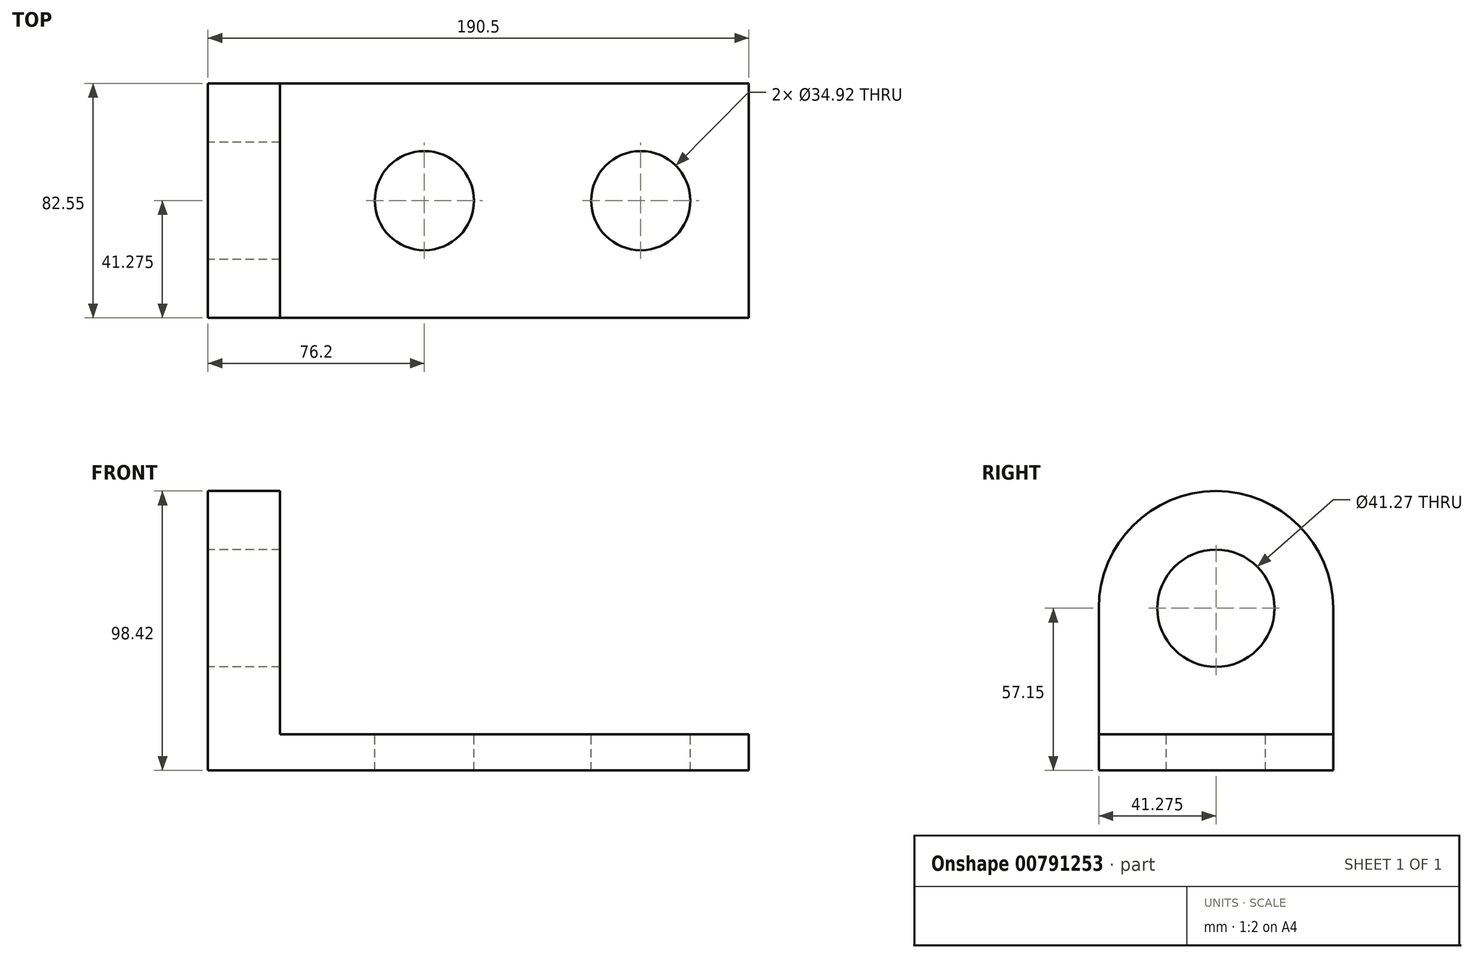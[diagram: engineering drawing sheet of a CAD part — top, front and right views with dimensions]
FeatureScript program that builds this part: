
annotation { "Feature Type Name" : "Feature", "Feature Type Description" : "" }
export const myFeature = defineFeature(function(context is Context, id is Id, definition is map)
    precondition{}
    {
        {
            var Q0;
            Q0=qCreatedBy(makeId("Front.planeOp"),FACE);
            var sketch = newSketch(context, id + "F0", { "sketchPlane" : qUnion([Q0])});
            skLineSegment(sketch, "E0", {"start": v(0, 0) * mm, "end": v(190.5, 0) * mm});
            skLineSegment(sketch, "E1", {"start": v(190.5, 0) * mm, "end": v(190.5, 12.7) * mm});
            skLineSegment(sketch, "E2", {"start": v(190.5, 12.7) * mm, "end": v(25.4, 12.7) * mm});
            skLineSegment(sketch, "E3", {"start": v(25.4, 12.7) * mm, "end": v(25.4, 165.1) * mm});
            skLineSegment(sketch, "E4", {"start": v(25.4, 165.1) * mm, "end": v(0, 165.1) * mm});
            skLineSegment(sketch, "E5", {"start": v(0, 165.1) * mm, "end": v(0, 0) * mm});
            skSolve(sketch);
        }
        {
            var Q0;
            Q0=makeQuery(id+"F0.imprint","IMPRINT",FACE,{"disambiguationData":[TD([[makeQuery(id+"F0.imprint","IMPRINT",EDGE,{"derivedFrom":sQuery(id+"F0.wireOp",EDGE,"E0")}),1.0]])]});
            extrude(context, id + "F1", {"entities" : qUnion([Q0]), "depth" : 82.55 * mm, "offsetDistance" : 25.4 * mm});
        }
        {
            var Q0;
            Q0=makeQuery(id+"F1.opExtrude","SWEPT_FACE",FACE,{"disambiguationData":[OSD([sQuery(id+"F0.wireOp",EDGE,"E5")])]});
            var sketch = newSketch(context, id + "F2", { "sketchPlane" : qUnion([Q0])});
            skLineSegment(sketch, "E6", {"start": v(0, 0) * mm, "end": v(0, 57.15) * mm, "construction": true});
            skLineSegment(sketch, "E7", {"start": v(0, 57.15) * mm, "end": v(82.55, 57.15) * mm, "construction": true});
            skLineSegment(sketch, "E8", {"start": v(82.55, 57.15) * mm, "end": v(82.55, 0) * mm, "construction": true});
            skArc(sketch, "E9", {"start": v(82.55, 57.15) * mm, "mid": v(41.28, 98.43) * mm, "end": v(0, 57.15) * mm});
            skSolve(sketch);
        }
        {
            var Q0;
            {var subQ0=sQuery(id+"F2.wireOp",EDGE,"E9");Q0=makeQuery(id+"F2.imprint","IMPRINT",FACE,{"disambiguationData":[TD([[makeQuery(id+"F2.imprint","IMPRINT",EDGE,{"derivedFrom":subQ0}),-1.0]])]});}
            extrude(context, id + "F3", {"entities" : qUnion([Q0]), "operationType" : NewBodyOperationType.REMOVE, "endBound" : BoundingType.UP_TO_NEXT, "oppositeDirection" : true, "depth" : 25.4 * mm, "offsetDistance" : 25.4 * mm});
        }
        {
            var Q0;
            Q0=makeQuery(id+"F1.opExtrude","SWEPT_FACE",FACE,{"disambiguationData":[OSD([sQuery(id+"F0.wireOp",EDGE,"E5")])]});
            var sketch = newSketch(context, id + "F4", { "sketchPlane" : qUnion([Q0])});
            skLineSegment(sketch, "E10", {"start": v(0, 0) * mm, "end": v(0, 57.15) * mm, "construction": true});
            skLineSegment(sketch, "E11", {"start": v(0, 57.15) * mm, "end": v(82.55, 57.15) * mm, "construction": true});
            skCircle(sketch, "E12", {"center": v(41.28, 57.15) * mm, "radius": 20.64 * mm});
            skSolve(sketch);
        }
        {
            var Q0;
            Q0=makeQuery(id+"F4.imprint","IMPRINT",FACE,{"disambiguationData":[TD([[makeQuery(id+"F4.imprint","IMPRINT",EDGE,{"derivedFrom":sQuery(id+"F4.wireOp",EDGE,"E12")}),1.0]])]});
            extrude(context, id + "F5", {"entities" : qUnion([Q0]), "operationType" : NewBodyOperationType.REMOVE, "endBound" : BoundingType.UP_TO_NEXT, "oppositeDirection" : true, "depth" : 25.4 * mm, "offsetDistance" : 25.4 * mm});
        }
        {
            var Q0;
            Q0=makeQuery(id+"F1.opExtrude","SWEPT_FACE",FACE,{"disambiguationData":[OSD([sQuery(id+"F0.wireOp",EDGE,"E2")])]});
            var sketch = newSketch(context, id + "F6", { "sketchPlane" : qUnion([Q0])});
            skLineSegment(sketch, "E13", {"start": v(25.4, -41.28) * mm, "end": v(76.2, -41.28) * mm, "construction": true});
            skLineSegment(sketch, "E14", {"start": v(76.2, -41.28) * mm, "end": v(152.4, -41.27) * mm, "construction": true});
            skCircle(sketch, "E15", {"center": v(76.2, -41.28) * mm, "radius": 17.46 * mm});
            skCircle(sketch, "E16", {"center": v(152.4, -41.27) * mm, "radius": 17.46 * mm});
            skSolve(sketch);
        }
        {
            var Q0;
            Q0=makeQuery(id+"F6.imprint","IMPRINT",FACE,{"disambiguationData":[TD([[makeQuery(id+"F6.imprint","IMPRINT",EDGE,{"derivedFrom":sQuery(id+"F6.wireOp",EDGE,"E15")}),1.0]])]});
            var Q1;
            Q1=makeQuery(id+"F6.imprint","IMPRINT",FACE,{"disambiguationData":[TD([[makeQuery(id+"F6.imprint","IMPRINT",EDGE,{"derivedFrom":sQuery(id+"F6.wireOp",EDGE,"E16")}),1.0]])]});
            extrude(context, id + "F7", {"entities" : qUnion([Q0, Q1]), "operationType" : NewBodyOperationType.REMOVE, "endBound" : BoundingType.UP_TO_NEXT, "oppositeDirection" : true, "depth" : 25.4 * mm, "offsetDistance" : 25.4 * mm});
        }
    });
